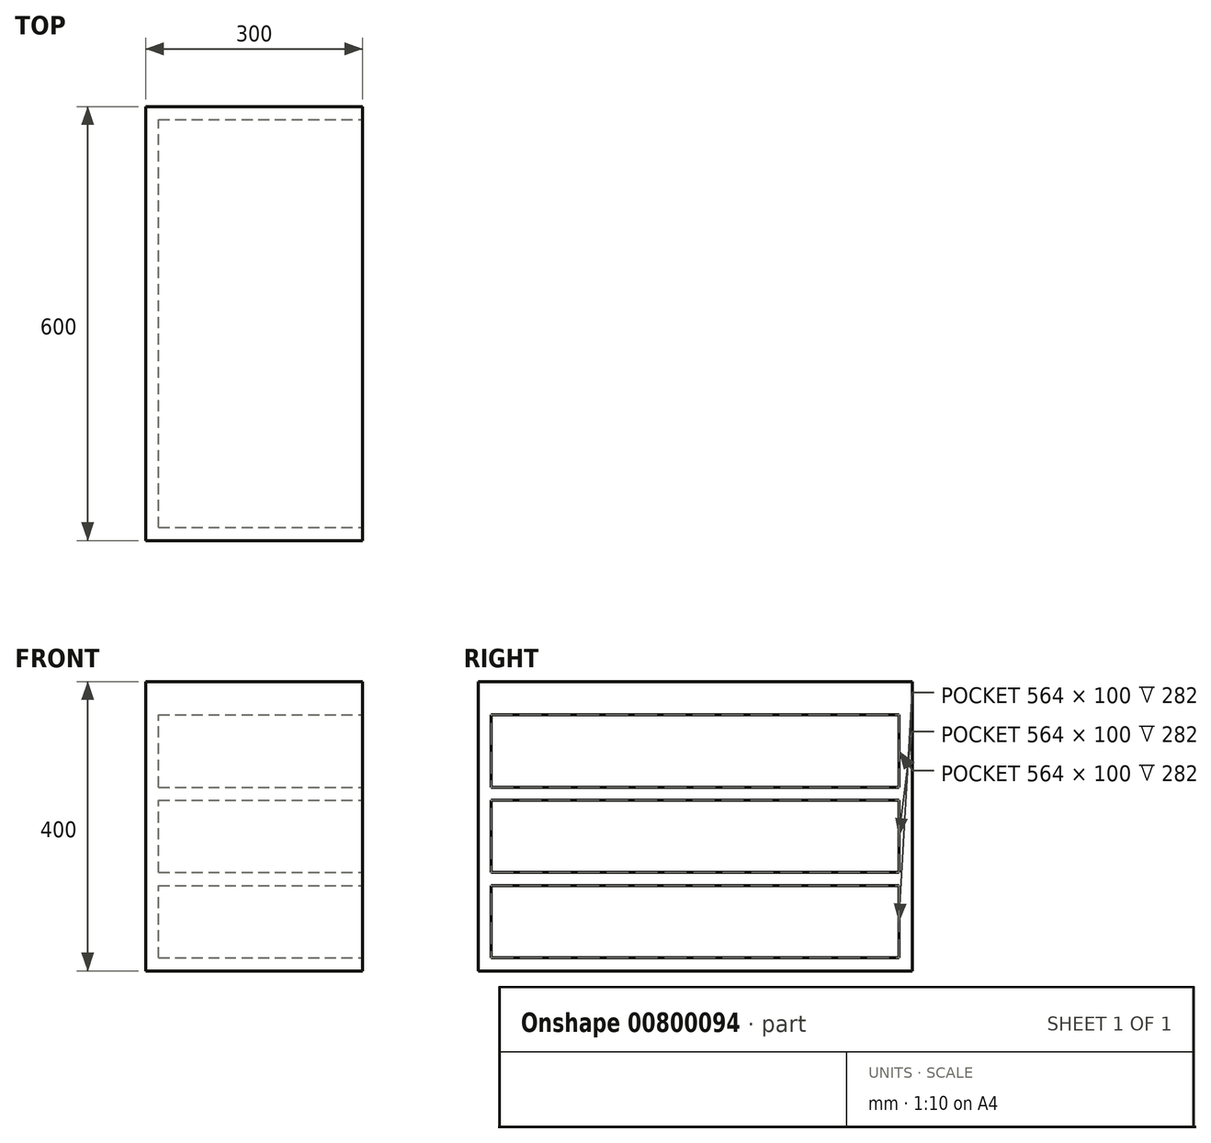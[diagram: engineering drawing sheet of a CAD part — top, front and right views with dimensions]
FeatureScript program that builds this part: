
annotation { "Feature Type Name" : "Feature", "Feature Type Description" : "" }
export const myFeature = defineFeature(function(context is Context, id is Id, definition is map)
    precondition{}
    {
        {
            var Q0;
            Q0=qCreatedBy(makeId("Right.planeOp"),FACE);
            var sketch = newSketch(context, id + "F0", { "sketchPlane" : qUnion([Q0])});
            skLineSegment(sketch, "E0", {"start": v(0, 3.9) * mm, "end": v(300, 3.9) * mm});
            skLineSegment(sketch, "E1", {"start": v(300, 3.9) * mm, "end": v(300, 403.9) * mm});
            skLineSegment(sketch, "E2", {"start": v(300, 403.9) * mm, "end": v(-300, 403.9) * mm});
            skLineSegment(sketch, "E3", {"start": v(0, 3.9) * mm, "end": v(-300, 3.9) * mm});
            skLineSegment(sketch, "E4", {"start": v(-300, 3.9) * mm, "end": v(-300, 403.9) * mm});
            skSolve(sketch);
        }
        {
            var Q0;
            Q0=makeQuery(id+"F0.imprint","IMPRINT",FACE,{"disambiguationData":[TD([[makeQuery(id+"F0.imprint","IMPRINT",EDGE,{"derivedFrom":sQuery(id+"F0.wireOp",EDGE,"E0")}),1.0]])]});
            extrude(context, id + "F1", {"entities" : qUnion([Q0]), "oppositeDirection" : true, "depth" : 300 * mm, "offsetDistance" : 25 * mm});
        }
        {
            var Q0;
            Q0=makeQuery(id+"F1.opExtrude","CAP_FACE",FACE,{"disambiguationData":[OSD([sQuery(id+"F0.wireOp",EDGE,"E0"),sQuery(id+"F0.wireOp",EDGE,"E1"),sQuery(id+"F0.wireOp",EDGE,"E2"),sQuery(id+"F0.wireOp",EDGE,"E3"),sQuery(id+"F0.wireOp",EDGE,"E4")])],"isStart":true});
            var sketch = newSketch(context, id + "F2", { "sketchPlane" : qUnion([Q0])});
            skLineSegment(sketch, "E5.bottom", {"start": v(-282, 21.9) * mm, "end": v(282, 21.9) * mm});
            skLineSegment(sketch, "E5.top", {"start": v(-282, 121.9) * mm, "end": v(282, 121.9) * mm});
            skLineSegment(sketch, "E5.left", {"start": v(-282, 21.9) * mm, "end": v(-282, 121.9) * mm});
            skLineSegment(sketch, "E5.right", {"start": v(282, 21.9) * mm, "end": v(282, 121.9) * mm});
            skLineSegment(sketch, "E6.0.1.0", {"start": v(282, 139.9) * mm, "end": v(282, 239.9) * mm});
            skLineSegment(sketch, "E6.0.1.1", {"start": v(-282, 139.9) * mm, "end": v(-282, 239.9) * mm});
            skLineSegment(sketch, "E6.0.1.2", {"start": v(-282, 239.9) * mm, "end": v(282, 239.9) * mm});
            skLineSegment(sketch, "E6.0.1.3", {"start": v(-282, 139.9) * mm, "end": v(282, 139.9) * mm});
            skLineSegment(sketch, "E6.0.2.0", {"start": v(282, 257.9) * mm, "end": v(282, 357.9) * mm});
            skLineSegment(sketch, "E6.0.2.1", {"start": v(-282, 257.9) * mm, "end": v(-282, 357.9) * mm});
            skLineSegment(sketch, "E6.0.2.2", {"start": v(-282, 357.9) * mm, "end": v(282, 357.9) * mm});
            skLineSegment(sketch, "E6.0.2.3", {"start": v(-282, 257.9) * mm, "end": v(282, 257.9) * mm});
            skLineSegment(sketch, "E6.direction1", {"start": v(-282, 21.9) * mm, "end": v(-257, 21.9) * mm, "construction": true});
            skLineSegment(sketch, "E6.direction2", {"start": v(-282, 21.9) * mm, "end": v(-282, 139.9) * mm, "construction": true});
            skSolve(sketch);
        }
        {
            var Q0;
            Q0=makeQuery(id+"F2.imprint","IMPRINT",FACE,{"disambiguationData":[TD([[makeQuery(id+"F2.imprint","IMPRINT",EDGE,{"derivedFrom":sQuery(id+"F2.wireOp",EDGE,"E6.0.2.0")}),1.0]])]});
            var Q1;
            Q1=makeQuery(id+"F2.imprint","IMPRINT",FACE,{"disambiguationData":[TD([[makeQuery(id+"F2.imprint","IMPRINT",EDGE,{"derivedFrom":sQuery(id+"F2.wireOp",EDGE,"E6.0.1.0")}),1.0]])]});
            var Q2;
            Q2=makeQuery(id+"F2.imprint","IMPRINT",FACE,{"disambiguationData":[TD([[makeQuery(id+"F2.imprint","IMPRINT",EDGE,{"derivedFrom":sQuery(id+"F2.wireOp",EDGE,"E5.bottom")}),1.0]])]});
            extrude(context, id + "F3", {"entities" : qUnion([Q0, Q1, Q2]), "operationType" : NewBodyOperationType.REMOVE, "oppositeDirection" : true, "depth" : (300 - 18) * mm, "hasOffset" : true, "offsetDistance" : -18 * mm});
        }
    });
